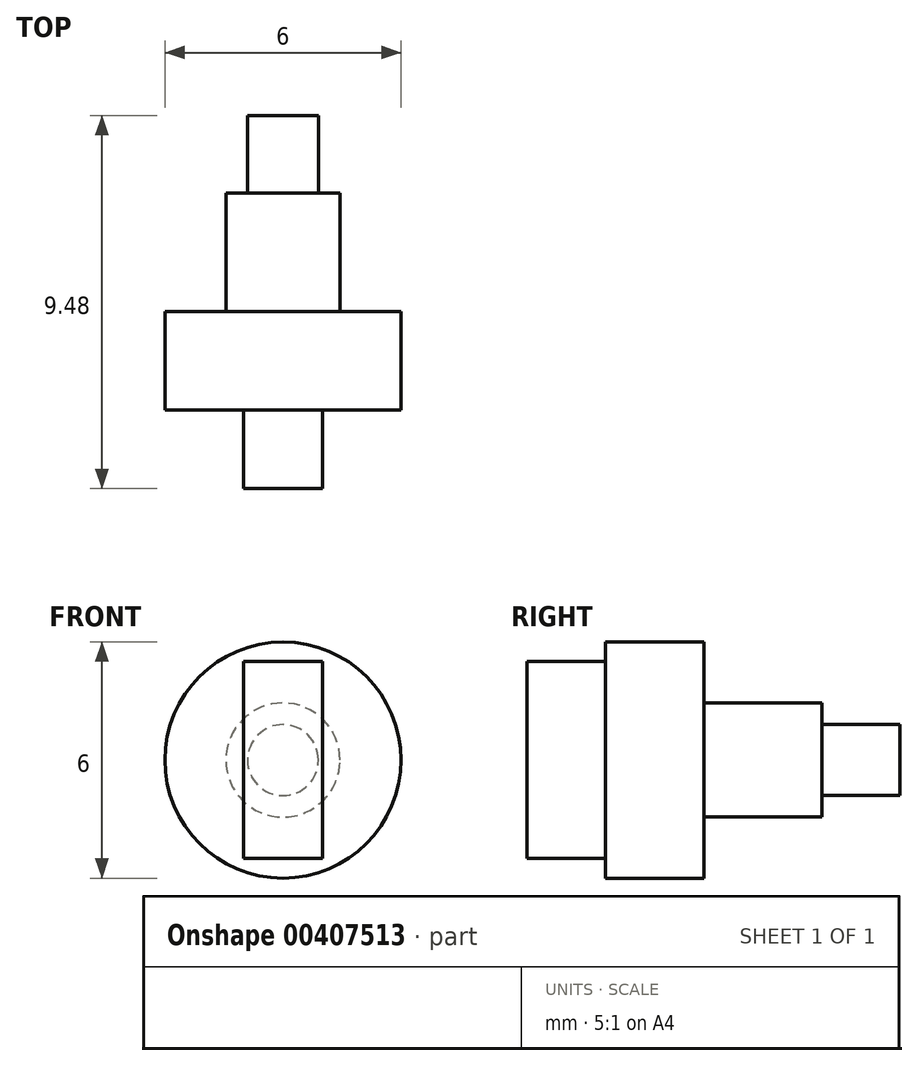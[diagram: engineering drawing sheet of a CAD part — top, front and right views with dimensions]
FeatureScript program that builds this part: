
annotation { "Feature Type Name" : "Feature", "Feature Type Description" : "" }
export const myFeature = defineFeature(function(context is Context, id is Id, definition is map)
    precondition{}
    {
        {
            var Q0;
            Q0=qCreatedBy(makeId("Front.planeOp"),FACE);
            var sketch = newSketch(context, id + "F0", { "sketchPlane" : qUnion([Q0])});
            skCircle(sketch, "E0", {"center": v(0, 0) * mm, "radius": 1.45 * mm});
            skSolve(sketch);
        }
        {
            var Q0;
            Q0 = qSketchRegion(id + "F0", true);
            extrude(context, id + "F1", {"entities" : qUnion([Q0]), "depth" : 3 * mm});
        }
        {
            var Q0;
            Q0=makeQuery(id+"F1.opExtrude","CAP_FACE",FACE,{"disambiguationData":[OSD([sQuery(id+"F0.wireOp",EDGE,"E0")])],"isStart":false});
            var sketch = newSketch(context, id + "F2", { "sketchPlane" : qUnion([Q0])});
            skCircle(sketch, "E1", {"center": v(0, 0) * mm, "radius": 3 * mm});
            skSolve(sketch);
        }
        {
            var Q0;
            Q0 = qSketchRegion(id + "F2", true);
            extrude(context, id + "F3", {"entities" : qUnion([Q0]), "operationType" : NewBodyOperationType.ADD, "depth" : 2.5 * mm});
        }
        {
            var Q0;
            Q0=makeQuery(id+"F1.opExtrude","CAP_FACE",FACE,{"disambiguationData":[OSD([sQuery(id+"F0.wireOp",EDGE,"E0")])],"isStart":true});
            var sketch = newSketch(context, id + "F4", { "sketchPlane" : qUnion([Q0])});
            skCircle(sketch, "E2", {"center": v(0, 0) * mm, "radius": 0.9 * mm});
            skSolve(sketch);
        }
        {
            var Q0;
            Q0 = qSketchRegion(id + "F4", true);
            extrude(context, id + "F5", {"entities" : qUnion([Q0]), "operationType" : NewBodyOperationType.ADD, "depth" : 1.98 * mm});
        }
        {
            var Q0;
            Q0=makeQuery(id+"F3.opExtrude","CAP_FACE",FACE,{"disambiguationData":[OSD([sQuery(id+"F2.wireOp",EDGE,"E1")])],"isStart":false});
            var sketch = newSketch(context, id + "F6", { "sketchPlane" : qUnion([Q0])});
            skLineSegment(sketch, "E3.bottom", {"start": v(1, -2.5) * mm, "end": v(-1, -2.5) * mm});
            skLineSegment(sketch, "E3.top", {"start": v(1, 2.5) * mm, "end": v(-1, 2.5) * mm});
            skLineSegment(sketch, "E3.left", {"start": v(1, -2.5) * mm, "end": v(1, 2.5) * mm});
            skLineSegment(sketch, "E3.right", {"start": v(-1, -2.5) * mm, "end": v(-1, 2.5) * mm});
            skPoint(sketch, "E3.middle", {"position": v(0, 0) * mm});
            skSolve(sketch);
        }
        {
            var Q0;
            Q0 = qSketchRegion(id + "F6", true);
            extrude(context, id + "F7", {"entities" : qUnion([Q0]), "operationType" : NewBodyOperationType.ADD, "depth" : 2 * mm});
        }
    });
